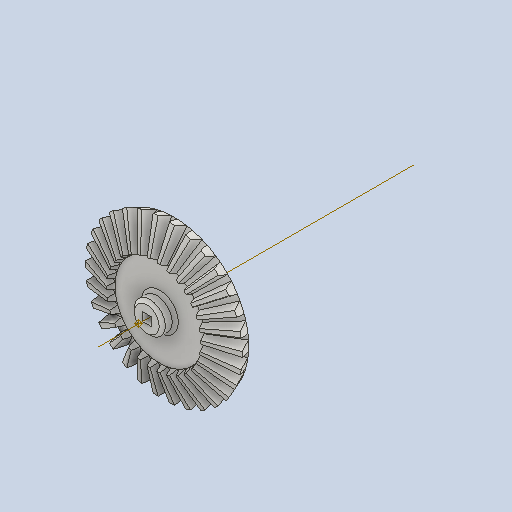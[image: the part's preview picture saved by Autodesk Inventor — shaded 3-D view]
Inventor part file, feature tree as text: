
AUTODESK INVENTOR PART (.ipt)
format: ipt  version: 2022 (Build 260153000, 153)  size: 713,728 bytes
history: native  units: in
note: dims shown in document units (in); Inventor stores cm internally (conversion verified against a paired STEP export)
features: other x30, sketch x3
ambient origin geometry x8: Origin, YZ Plane, XZ Plane, XY Plane, X Axis, Y Axis, Z Axis, Center Point
bodies: Solid1 (feature_tree)
feature tree (33):
  other  "Bevel Gear21_MIR1.ipt"
  other  "Solid1::Bevel Gear21_MIR1.ipt"
  other  "TaggingFeature1"
  other  "Teeth Body Sketch"
  other  "Start Sketch"
  other  "End Sketch"
  other  "End Sketch Right"
  other  "End Sketch Left"
  other  "Body Sketch"
  sketch  "Sketch6"  dims[d0=0.3937in]
  sketch  "Sketch8"  dims[d48=0.0in]
  sketch  "Sketch9"  dims[d49=0.0in d50=90.0deg d52=0.0in d53=0.0in d54=0.0in]
  other  "3D Sketch Right"
  other  "3D Sketch Left"
  other  "Mesh Plane"
  other  "Top Plane"
  other  "Mesh Plane2"
  other  "Tooth Plane"
  other  "End Plane"
  other  "End Plane Right"
  other  "End Plane Left"
  other  "Z Axis_1"
  other  "Top Point"
  other  "Start Point"
  other  "End Point"
  other  "Srf1"
  other  "Srf1::Derived"
  other  "Start plane iMate"
  other  "Mesh iMate2"
  other  "Axis Angle iMate"
  other  "Axis iMate"
  other  "Mesh iMate"
  other  "Intersection iMate"
